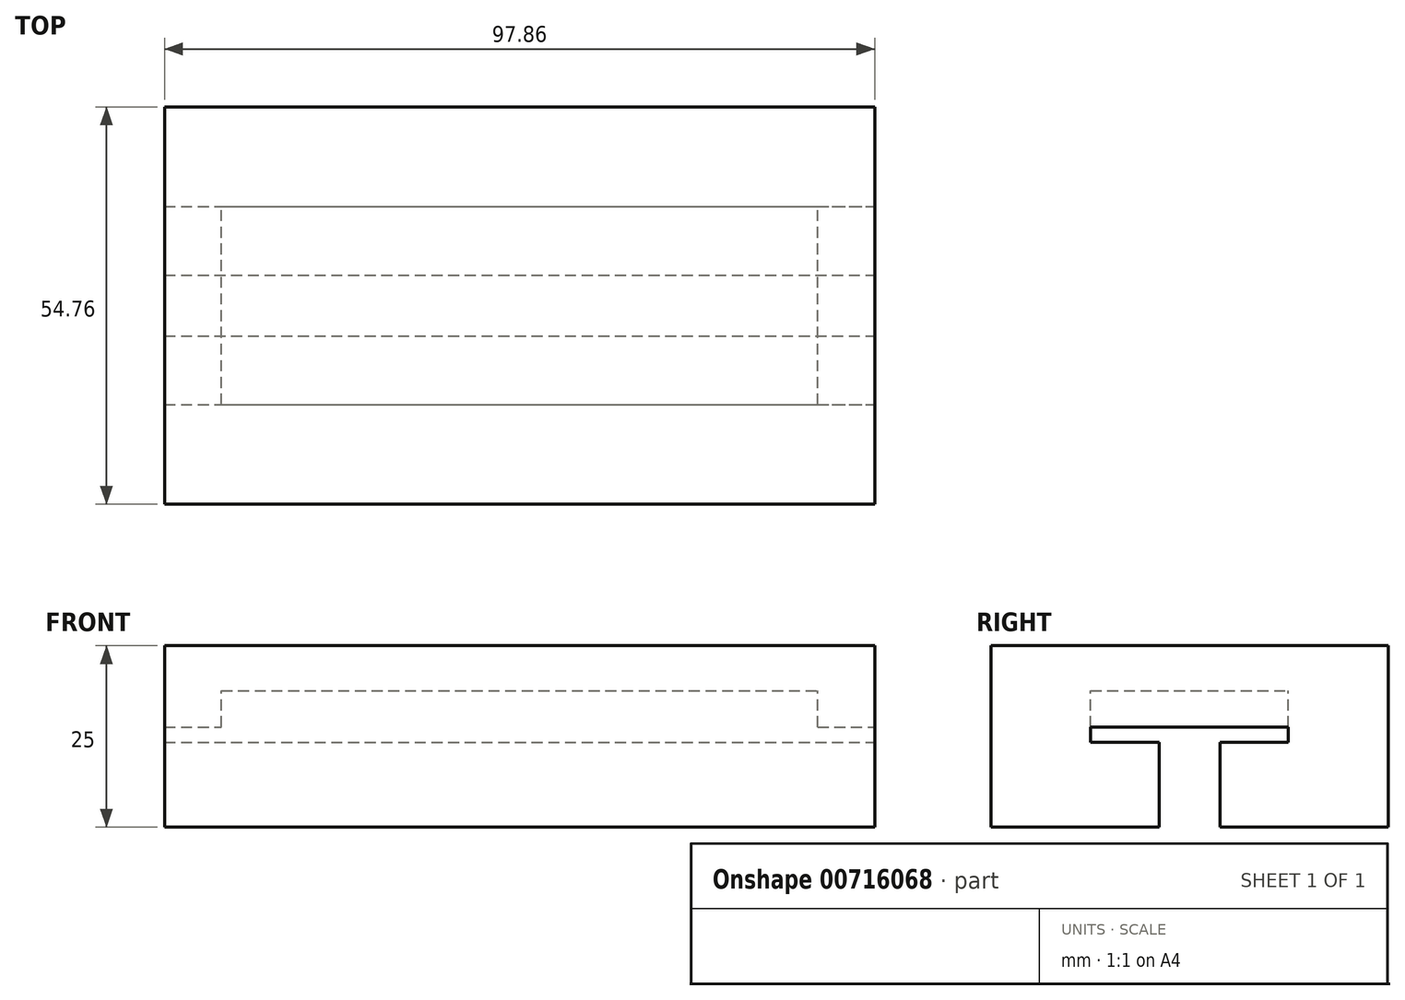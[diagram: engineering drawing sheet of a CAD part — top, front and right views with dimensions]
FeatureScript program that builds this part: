
annotation { "Feature Type Name" : "Feature", "Feature Type Description" : "" }
export const myFeature = defineFeature(function(context is Context, id is Id, definition is map)
    precondition{}
    {
        {
            var Q0;
            Q0=qCreatedBy(makeId("Top.planeOp"),FACE);
            var sketch = newSketch(context, id + "F0", { "sketchPlane" : qUnion([Q0])});
            skLineSegment(sketch, "E0.bottom", {"start": v(48.93, 27.38) * mm, "end": v(-48.93, 27.38) * mm});
            skLineSegment(sketch, "E0.top", {"start": v(48.93, -27.38) * mm, "end": v(-48.93, -27.38) * mm});
            skLineSegment(sketch, "E0.left", {"start": v(48.93, 27.38) * mm, "end": v(48.93, -27.38) * mm});
            skLineSegment(sketch, "E0.right", {"start": v(-48.93, 27.38) * mm, "end": v(-48.93, -27.38) * mm});
            skPoint(sketch, "E0.middle", {"position": v(0, 0) * mm});
            skLineSegment(sketch, "E1.bottom", {"start": v(-48.93, -6) * mm, "end": v(-17.32, -6) * mm});
            skLineSegment(sketch, "E1.top", {"start": v(-48.93, 6) * mm, "end": v(-17.32, 6) * mm});
            skLineSegment(sketch, "E1.left", {"start": v(-48.93, -6) * mm, "end": v(-48.93, 6) * mm});
            skLineSegment(sketch, "E1.right", {"start": v(-17.32, -6) * mm, "end": v(-17.32, 6) * mm});
            skSolve(sketch);
        }
        {
            var Q0;
            {var subQ1=sQuery(id+"F0.wireOp",EDGE,"E0.bottom");Q0=makeQuery(id+"F0.imprint","IMPRINT",FACE,{"disambiguationData":[TD([[makeQuery(id+"F0.imprint","IMPRINT",EDGE,{"derivedFrom":subQ1}),1.0]])]});}
            var Q1;
            Q1=makeQuery(id+"F0.imprint","IMPRINT",FACE,{"disambiguationData":[TD([[makeQuery(id+"F0.imprint","IMPRINT",EDGE,{"derivedFrom":sQuery(id+"F0.wireOp",EDGE,"E1.bottom")}),1.0]])]});
            extrude(context, id + "F1", {"entities" : qUnion([Q0, Q1]), "depth" : 25 * mm, "offsetDistance" : 25 * mm});
        }
        {
            var Q0;
            Q0=makeQuery(id+"F1.opExtrude","SWEPT_FACE",FACE,{"disambiguationData":[OSD([sQuery(id+"F0.wireOp",EDGE,"E0.left")])]});
            var sketch = newSketch(context, id + "F2", { "sketchPlane" : qUnion([Q0])});
            skLineSegment(sketch, "E2.bottom", {"start": v(13.63, 18.8) * mm, "end": v(-13.63, 18.8) * mm});
            skLineSegment(sketch, "E2.top", {"start": v(13.63, 11.67) * mm, "end": v(4.19, 11.67) * mm});
            skLineSegment(sketch, "E2.left", {"start": v(13.63, 18.8) * mm, "end": v(13.63, 11.67) * mm});
            skLineSegment(sketch, "E2.right", {"start": v(-13.63, 18.8) * mm, "end": v(-13.63, 11.67) * mm});
            skPoint(sketch, "E2.middle", {"position": v(0, 15.23) * mm});
            skLineSegment(sketch, "E3.bottom", {"start": v(4.19, -14.7) * mm, "end": v(-4.19, -14.7) * mm});
            skLineSegment(sketch, "E3.left", {"start": v(4.19, -14.7) * mm, "end": v(4.19, 11.67) * mm});
            skLineSegment(sketch, "E3.right", {"start": v(-4.19, -14.7) * mm, "end": v(-4.19, 11.67) * mm});
            skPoint(sketch, "E3.middle", {"position": v(0, 0) * mm});
            skPoint(sketch, "E4.orphan", {"position": v(4.19, 14.7) * mm});
            skPoint(sketch, "E5.orphan", {"position": v(-4.19, 14.7) * mm});
            skLineSegment(sketch, "E6.trimOffspring", {"start": v(-4.19, 11.67) * mm, "end": v(-13.63, 11.67) * mm});
            skSolve(sketch);
        }
        {
            var Q0;
            {var subQ0=sQuery(id+"F2.wireOp",EDGE,"E3.bottom");Q0=makeQuery(id+"F2.imprint","IMPRINT",FACE,{"disambiguationData":[TD([[makeQuery(id+"F2.imprint","IMPRINT",EDGE,{"derivedFrom":subQ0}),-1.0]])]});}
            var Q1;
            Q1=makeQuery(id+"F2.imprint","IMPRINT",FACE,{"disambiguationData":[TD([[makeQuery(id+"F2.imprint","IMPRINT",EDGE,{"derivedFrom":sQuery(id+"F2.wireOp",EDGE,"E2.bottom")}),1.0]])]});
            extrude(context, id + "F3", {"entities" : qUnion([Q0, Q1]), "operationType" : NewBodyOperationType.REMOVE, "endBound" : BoundingType.UP_TO_NEXT, "oppositeDirection" : true, "depth" : 25 * mm, "offsetDistance" : 25 * mm});
        }
        {
            var Q0;
            Q0=makeQuery(id+"F3.boolean.opBoolean","COPY",FACE,{"derivedFrom":makeQuery(id+"F3.opExtrude","SWEPT_FACE",FACE,{"disambiguationData":[OSD([sQuery(id+"F2.wireOp",EDGE,"E2.bottom")])]})});
            var sketch = newSketch(context, id + "F4", { "sketchPlane" : qUnion([Q0])});
            skLineSegment(sketch, "E7.bottom", {"start": v(-48.93, 13.63) * mm, "end": v(-41.08, 13.63) * mm});
            skLineSegment(sketch, "E7.top", {"start": v(-48.93, -13.63) * mm, "end": v(-41.08, -13.63) * mm});
            skLineSegment(sketch, "E7.left", {"start": v(-48.93, 13.63) * mm, "end": v(-48.93, -13.63) * mm});
            skLineSegment(sketch, "E7.right", {"start": v(-41.08, 13.63) * mm, "end": v(-41.08, -13.63) * mm});
            skLineSegment(sketch, "E8.MirrorCS", {"start": v(41.08, 13.63) * mm, "end": v(41.08, -13.63) * mm});
            skLineSegment(sketch, "E9.MirrorCS", {"start": v(48.93, 13.63) * mm, "end": v(41.08, 13.63) * mm});
            skLineSegment(sketch, "E10.MirrorCS", {"start": v(48.93, 13.63) * mm, "end": v(48.93, -13.63) * mm});
            skLineSegment(sketch, "E11.MirrorCS", {"start": v(48.93, -13.63) * mm, "end": v(41.08, -13.63) * mm});
            skSolve(sketch);
        }
        {
            var Q0;
            Q0 = qSketchRegion(id + "F4", true);
            extrude(context, id + "F5", {"entities" : qUnion([Q0]), "operationType" : NewBodyOperationType.ADD, "depth" : 5 * mm, "offsetDistance" : 25 * mm});
        }
    });
